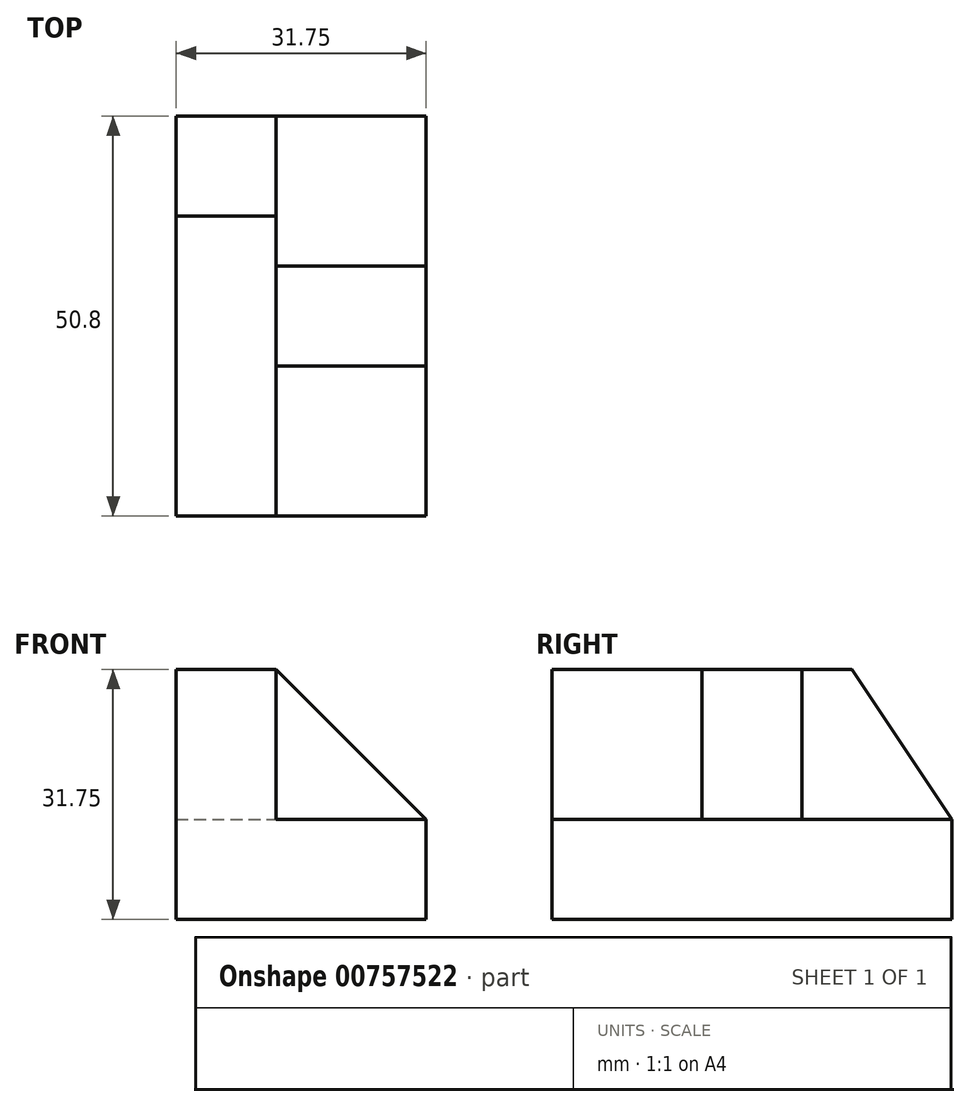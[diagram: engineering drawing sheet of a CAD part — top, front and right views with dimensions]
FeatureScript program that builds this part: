
annotation { "Feature Type Name" : "Feature", "Feature Type Description" : "" }
export const myFeature = defineFeature(function(context is Context, id is Id, definition is map)
    precondition{}
    {
        {
            var Q0;
            Q0=qCreatedBy(makeId("Right.planeOp"),FACE);
            var sketch = newSketch(context, id + "F0", { "sketchPlane" : qUnion([Q0])});
            skLineSegment(sketch, "E0", {"start": v(0, 0) * mm, "end": v(0, 31.75) * mm});
            skLineSegment(sketch, "E1", {"start": v(0, 31.75) * mm, "end": v(-50.8, 31.75) * mm});
            skLineSegment(sketch, "E2", {"start": v(-50.8, 31.75) * mm, "end": v(-50.8, 0) * mm});
            skLineSegment(sketch, "E3", {"start": v(-50.8, 0) * mm, "end": v(0, 0) * mm});
            skSolve(sketch);
        }
        {
            var Q0;
            Q0 = qSketchRegion(id + "F0", true);
            extrude(context, id + "F1", {"entities" : qUnion([Q0]), "depth" : 31.75 * mm, "offsetDistance" : 25.4 * mm});
        }
        {
            var Q0;
            Q0=makeQuery(id+"F1.opExtrude","SWEPT_FACE",FACE,{"disambiguationData":[OSD([sQuery(id+"F0.wireOp",EDGE,"E0")])]});
            var sketch = newSketch(context, id + "F2", { "sketchPlane" : qUnion([Q0])});
            skLineSegment(sketch, "E4", {"start": v(-12.7, 31.75) * mm, "end": v(-12.7, 12.7) * mm});
            skLineSegment(sketch, "E5", {"start": v(-12.7, 12.7) * mm, "end": v(-31.75, 12.7) * mm});
            skSolve(sketch);
        }
        {
            var Q0;
            {var subQ0=sQuery(id+"F2.wireOp",EDGE,"E4");Q0=makeQuery(id+"F2.imprint","IMPRINT",FACE,{"disambiguationData":[TD([[makeQuery(id+"F2.imprint","IMPRINT",EDGE,{"derivedFrom":subQ0}),-1.0]])]});}
            extrude(context, id + "F3", {"entities" : qUnion([Q0]), "operationType" : NewBodyOperationType.REMOVE, "endBound" : BoundingType.THROUGH_ALL, "oppositeDirection" : true, "depth" : 25.4 * mm, "offsetDistance" : 25.4 * mm});
        }
        {
            var Q0;
            Q0=makeQuery(id+"F3.boolean.opBoolean","COPY",FACE,{"derivedFrom":makeQuery(id+"F3.opExtrude","SWEPT_FACE",FACE,{"disambiguationData":[OSD([sQuery(id+"F2.wireOp",EDGE,"E4")])]})});
            var sketch = newSketch(context, id + "F4", { "sketchPlane" : qUnion([Q0])});
            skLineSegment(sketch, "E6", {"start": v(-12.7, 31.75) * mm, "end": v(0, 12.7) * mm});
            skSolve(sketch);
        }
        {
            var Q0;
            {var subQ0=sQuery(id+"F4.wireOp",EDGE,"E6");Q0=makeQuery(id+"F4.imprint","IMPRINT",FACE,{"disambiguationData":[TD([[makeQuery(id+"F4.imprint","IMPRINT",EDGE,{"derivedFrom":subQ0}),1.0]])]});}
            extrude(context, id + "F5", {"entities" : qUnion([Q0]), "operationType" : NewBodyOperationType.REMOVE, "endBound" : BoundingType.THROUGH_ALL, "oppositeDirection" : true, "depth" : 25.4 * mm, "offsetDistance" : 25.4 * mm});
        }
        {
            var Q0;
            Q0=makeQuery(id+"F3.boolean.opBoolean","COPY",FACE,{"derivedFrom":makeQuery(id+"F3.opExtrude","SWEPT_FACE",FACE,{"disambiguationData":[OSD([sQuery(id+"F2.wireOp",EDGE,"E4")])]})});
            var sketch = newSketch(context, id + "F6", { "sketchPlane" : qUnion([Q0])});
            skLineSegment(sketch, "E7", {"start": v(-19.05, 31.75) * mm, "end": v(-19.05, 12.7) * mm});
            skLineSegment(sketch, "E8", {"start": v(-19.05, 12.7) * mm, "end": v(-31.75, 12.7) * mm});
            skLineSegment(sketch, "E9", {"start": v(-31.75, 12.7) * mm, "end": v(-31.75, 31.75) * mm});
            skLineSegment(sketch, "E10", {"start": v(-31.75, 31.75) * mm, "end": v(-19.05, 31.75) * mm});
            skSolve(sketch);
        }
        {
            var Q0;
            Q0=makeQuery(id+"F6.imprint","IMPRINT",FACE,{"disambiguationData":[TD([[makeQuery(id+"F6.imprint","IMPRINT",EDGE,{"derivedFrom":sQuery(id+"F6.wireOp",EDGE,"E7")}),-1.0]])]});
            extrude(context, id + "F7", {"entities" : qUnion([Q0]), "operationType" : NewBodyOperationType.ADD, "depth" : 25.4 * mm, "offsetDistance" : 25.4 * mm});
        }
        {
            var Q0;
            Q0=makeQuery(id+"F7.opExtrude","SWEPT_FACE",FACE,{"disambiguationData":[OSD([sQuery(id+"F6.wireOp",EDGE,"E7")])]});
            var sketch = newSketch(context, id + "F8", { "sketchPlane" : qUnion([Q0])});
            skLineSegment(sketch, "E11", {"start": v(-31.75, 12.7) * mm, "end": v(-12.7, 31.75) * mm});
            skSolve(sketch);
        }
        {
            var Q0;
            Q0=makeQuery(id+"F8.imprint","IMPRINT",FACE,{"disambiguationData":[TD([[makeQuery(id+"F8.imprint","IMPRINT",EDGE,{"derivedFrom":sQuery(id+"F8.wireOp",EDGE,"E11")}),1.0]])]});
            extrude(context, id + "F9", {"entities" : qUnion([Q0]), "operationType" : NewBodyOperationType.REMOVE, "endBound" : BoundingType.THROUGH_ALL, "oppositeDirection" : true, "depth" : 25.4 * mm, "offsetDistance" : 25.4 * mm});
        }
    });
